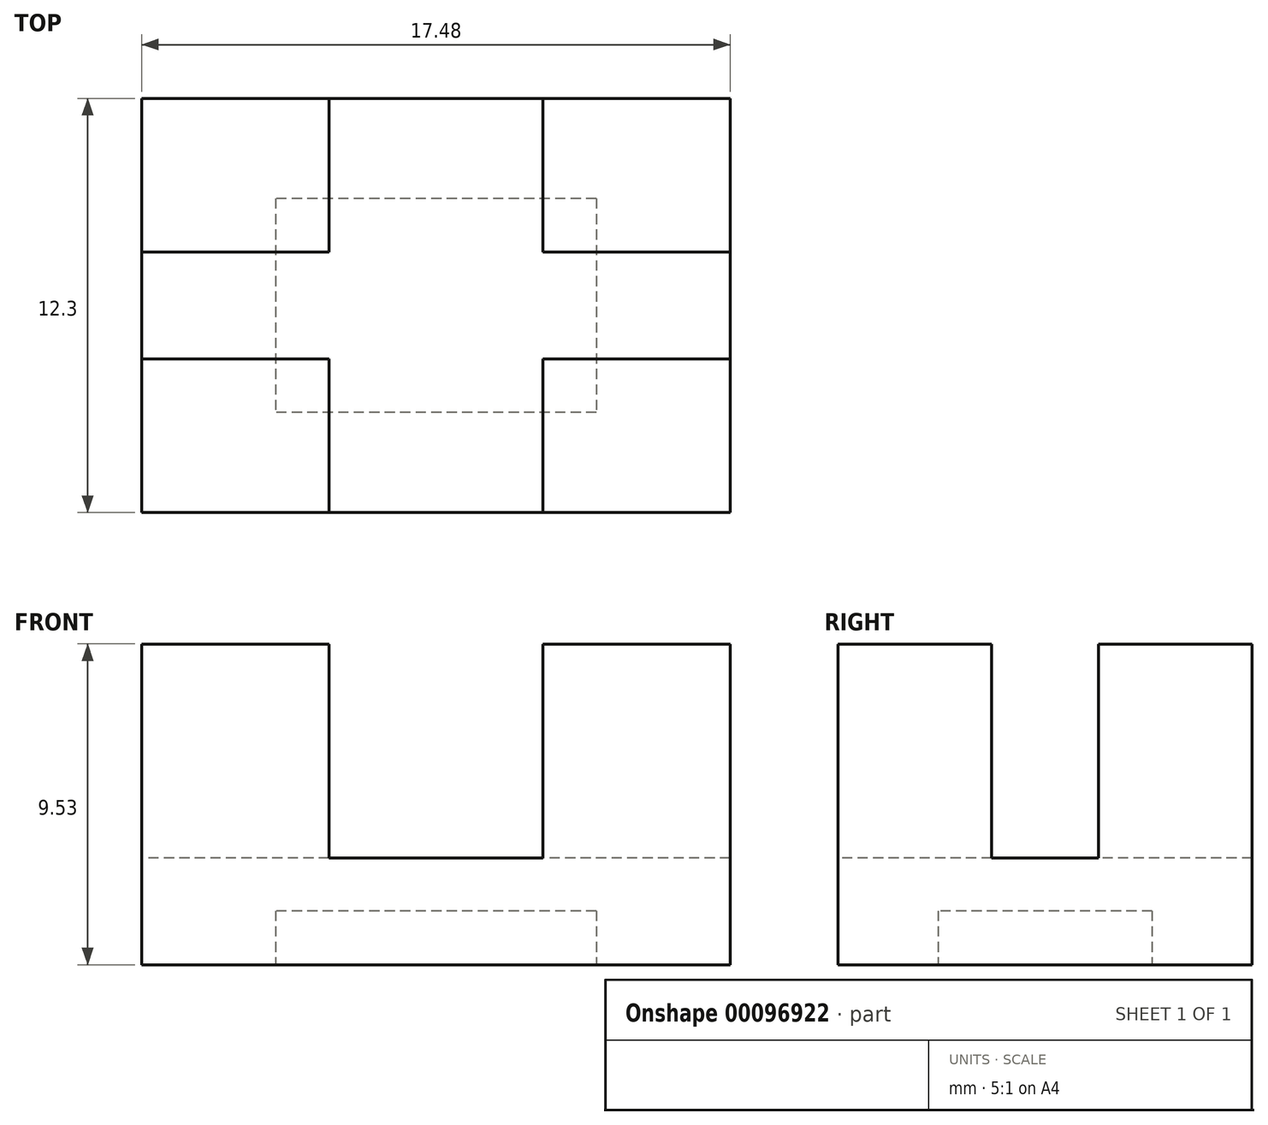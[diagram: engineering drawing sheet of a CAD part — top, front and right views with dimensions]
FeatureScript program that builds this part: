
annotation { "Feature Type Name" : "Feature", "Feature Type Description" : "" }
export const myFeature = defineFeature(function(context is Context, id is Id, definition is map)
    precondition{}
    {
        {
            var Q0;
            Q0=qCreatedBy(makeId("Top.planeOp"),FACE);
            var sketch = newSketch(context, id + "F0", { "sketchPlane" : qUnion([Q0])});
            skLineSegment(sketch, "E0.bottom", {"start": v(8.74, -6.15) * mm, "end": v(-8.74, -6.15) * mm});
            skLineSegment(sketch, "E0.top", {"start": v(8.74, 6.15) * mm, "end": v(-8.74, 6.15) * mm});
            skLineSegment(sketch, "E0.left", {"start": v(8.74, -6.15) * mm, "end": v(8.74, 6.15) * mm});
            skLineSegment(sketch, "E0.right", {"start": v(-8.74, -6.15) * mm, "end": v(-8.74, 6.15) * mm});
            skPoint(sketch, "E0.middle", {"position": v(0, 0) * mm});
            skSolve(sketch);
        }
        {
            var Q0;
            Q0=makeQuery(id+"F0.imprint","IMPRINT",FACE,{"disambiguationData":[TD([[makeQuery(id+"F0.imprint","IMPRINT",EDGE,{"derivedFrom":sQuery(id+"F0.wireOp",EDGE,"E0.bottom")}),-1.0]])]});
            extrude(context, id + "F1", {"entities" : qUnion([Q0]), "depth" : 9.52 * mm});
        }
        {
            var Q0;
            Q0=makeQuery(id+"F1.opExtrude","CAP_FACE",FACE,{"disambiguationData":[OSD([sQuery(id+"F0.wireOp",EDGE,"E0.bottom"),sQuery(id+"F0.wireOp",EDGE,"E0.top"),sQuery(id+"F0.wireOp",EDGE,"E0.left"),sQuery(id+"F0.wireOp",EDGE,"E0.right")])],"isStart":false});
            var sketch = newSketch(context, id + "F2", { "sketchPlane" : qUnion([Q0])});
            skLineSegment(sketch, "E1.bottom", {"start": v(3.17, 6.15) * mm, "end": v(-3.18, 6.15) * mm});
            skLineSegment(sketch, "E1.top", {"start": v(3.17, -6.15) * mm, "end": v(-3.18, -6.15) * mm});
            skLineSegment(sketch, "E1.left", {"start": v(3.17, 6.15) * mm, "end": v(3.17, -6.15) * mm});
            skLineSegment(sketch, "E1.right", {"start": v(-3.18, 6.15) * mm, "end": v(-3.18, -6.15) * mm});
            skPoint(sketch, "E1.middle", {"position": v(0, 0) * mm});
            skSolve(sketch);
        }
        {
            var Q0;
            Q0=makeQuery(id+"F2.imprint","IMPRINT",FACE,{"disambiguationData":[TD([[makeQuery(id+"F2.imprint","IMPRINT",EDGE,{"derivedFrom":sQuery(id+"F2.wireOp",EDGE,"E1.bottom")}),1.0]])]});
            extrude(context, id + "F3", {"entities" : qUnion([Q0]), "operationType" : NewBodyOperationType.REMOVE, "oppositeDirection" : true, "depth" : 6.35 * mm});
        }
        {
            var Q0;
            {var subQ0=sQuery(id+"F0.wireOp",EDGE,"E0.bottom");var subQ1=sQuery(id+"F0.wireOp",EDGE,"E0.top");var subQ2=sQuery(id+"F0.wireOp",EDGE,"E0.right");Q0=makeQuery(id+"F3.boolean.opBoolean","SPLIT",FACE,{"disambiguationData":[TD([makeQuery(id+"F1.opExtrude","SWEPT_FACE",FACE,{"disambiguationData":[OSD([subQ2])]})])],"derivedFrom":makeQuery(id+"F1.opExtrude","CAP_FACE",FACE,{"disambiguationData":[OSD([subQ0,subQ1,sQuery(id+"F0.wireOp",EDGE,"E0.left"),subQ2])],"isStart":false})});}
            var sketch = newSketch(context, id + "F4", { "sketchPlane" : qUnion([Q0])});
            skLineSegment(sketch, "E2.bottom", {"start": v(8.74, -1.59) * mm, "end": v(-8.74, -1.59) * mm});
            skLineSegment(sketch, "E2.top", {"start": v(8.74, 1.59) * mm, "end": v(-8.74, 1.59) * mm});
            skLineSegment(sketch, "E2.left", {"start": v(8.74, -1.59) * mm, "end": v(8.74, 1.59) * mm});
            skLineSegment(sketch, "E2.right", {"start": v(-8.74, -1.59) * mm, "end": v(-8.74, 1.59) * mm});
            skPoint(sketch, "E2.middle", {"position": v(0, 0) * mm});
            skSolve(sketch);
        }
        {
            var Q0;
            {var subQ0=sQuery(id+"F4.wireOp",EDGE,"E2.right");Q0=makeQuery(id+"F4.imprint","IMPRINT",FACE,{"disambiguationData":[TD([[makeQuery(id+"F4.imprint","IMPRINT",EDGE,{"derivedFrom":subQ0}),-1.0]])]});}
            var Q1;
            {var subQ0=sQuery(id+"F4.wireOp",EDGE,"E2.left");Q1=makeQuery(id+"F4.imprint","IMPRINT",FACE,{"disambiguationData":[TD([[makeQuery(id+"F4.imprint","IMPRINT",EDGE,{"derivedFrom":subQ0}),1.0]])]});}
            extrude(context, id + "F5", {"entities" : qUnion([Q0, Q1]), "operationType" : NewBodyOperationType.REMOVE, "oppositeDirection" : true, "depth" : 6.35 * mm});
        }
        {
            var Q0;
            Q0=makeQuery(id+"F1.opExtrude","CAP_FACE",FACE,{"disambiguationData":[OSD([sQuery(id+"F0.wireOp",EDGE,"E0.bottom"),sQuery(id+"F0.wireOp",EDGE,"E0.top"),sQuery(id+"F0.wireOp",EDGE,"E0.left"),sQuery(id+"F0.wireOp",EDGE,"E0.right")])],"isStart":true});
            var sketch = newSketch(context, id + "F6", { "sketchPlane" : qUnion([Q0])});
            skLineSegment(sketch, "E3.bottom", {"start": v(4.76, -3.18) * mm, "end": v(-4.76, -3.18) * mm});
            skLineSegment(sketch, "E3.top", {"start": v(4.76, 3.18) * mm, "end": v(-4.76, 3.18) * mm});
            skLineSegment(sketch, "E3.left", {"start": v(4.76, -3.18) * mm, "end": v(4.76, 3.17) * mm});
            skLineSegment(sketch, "E3.right", {"start": v(-4.76, -3.18) * mm, "end": v(-4.76, 3.17) * mm});
            skPoint(sketch, "E3.middle", {"position": v(0, 0) * mm});
            skSolve(sketch);
        }
        {
            var Q0;
            Q0=makeQuery(id+"F6.imprint","IMPRINT",FACE,{"disambiguationData":[TD([[makeQuery(id+"F6.imprint","IMPRINT",EDGE,{"derivedFrom":sQuery(id+"F6.wireOp",EDGE,"E3.bottom")}),-1.0]])]});
            extrude(context, id + "F7", {"entities" : qUnion([Q0]), "operationType" : NewBodyOperationType.REMOVE, "oppositeDirection" : true, "depth" : 1.6 * mm});
        }
    });
